# Revit family: Mop_Sink-Acorn-Terrazzo-Ware-TCR-28
name_source: partatom
category: Plumbing Fixtures
units: mm (PartAtom-declared; Revit-internal decimal feet)

## family parameters
Always vertical = No
Cut with Voids When Loaded = No
OmniClass Number = 23.45.05.14.14.27
OmniClass Title = Service Sinks
Part Type = Normal
Room Calculation Point = No
Round Connector Dimension = Use Diameter
Shared = Yes
Work Plane-Based = Yes

## types (1)
- TCR-28
    Assembly Code = D2010440
    BDS - Beehive Dome Strainer = No
    CW Connection = No
    CWFU = 3
    Default Elevation = 0"
    Description = 28" x 28" x 12" Height (1/4 Circle) Corner Terrazzo Mop Sink
    Drain Finish = Metal-Stern Williams-Stainless Steel
    Drain Length = 12"
    Drain Width = 12"
    Finish = Stone-Stern Williams-Terrazzo
    HW Connection = No
    HWFU = 3
    Height = 12"
    Installation Type = Floor Mounted
    KDG3 - Rubber Drain Gasket for 3" Waste Pipe = No
    KF - Tiling Flange(s) (Shipped Loose) = No
    KFC - Faucet, Chrome Finish (H&C) = No
    KH36 - Hose 36" Long with Wall Hanger = No
    KMH - Mop Hanger with 3 Grips on a Stainless Steel Bracket = No
    KWG - Wall Guard (Shipped Loose) = No
    LB - Lint Basket/Strainer = No
    Length = 28"
    Manufacturer = Acorn
    Material = Stone-Stern Williams-Terrazzo
    Model = TCR-28
    Product Documentation Link = https://www.acorneng.com
    Product Page URL = https://www.acorneng.com
    SSC - Stainless Steel Cap (requires -SH option) = No
    Stainlet Steel Cap = Metal-Stern Williams-Stainless Steel
    TF1 - Tiling Flange, Left = No
    TF1 - Tiling Flange, Right = No
    TF2 - Tiling Flange, Two Sides = No
    Tiling Flange = Metal-Stern Williams-Stainless Steel
    URL = https://www.acorneng.com
    Vent Connection = No
    WFU = 4
    Waste Connection = Yes
    Waste Connection Diameter = 3"
    Width = 28"

## geometry (parser evidence)
native form markers: Sweep x2
no freeform markers — native parametric forms only
